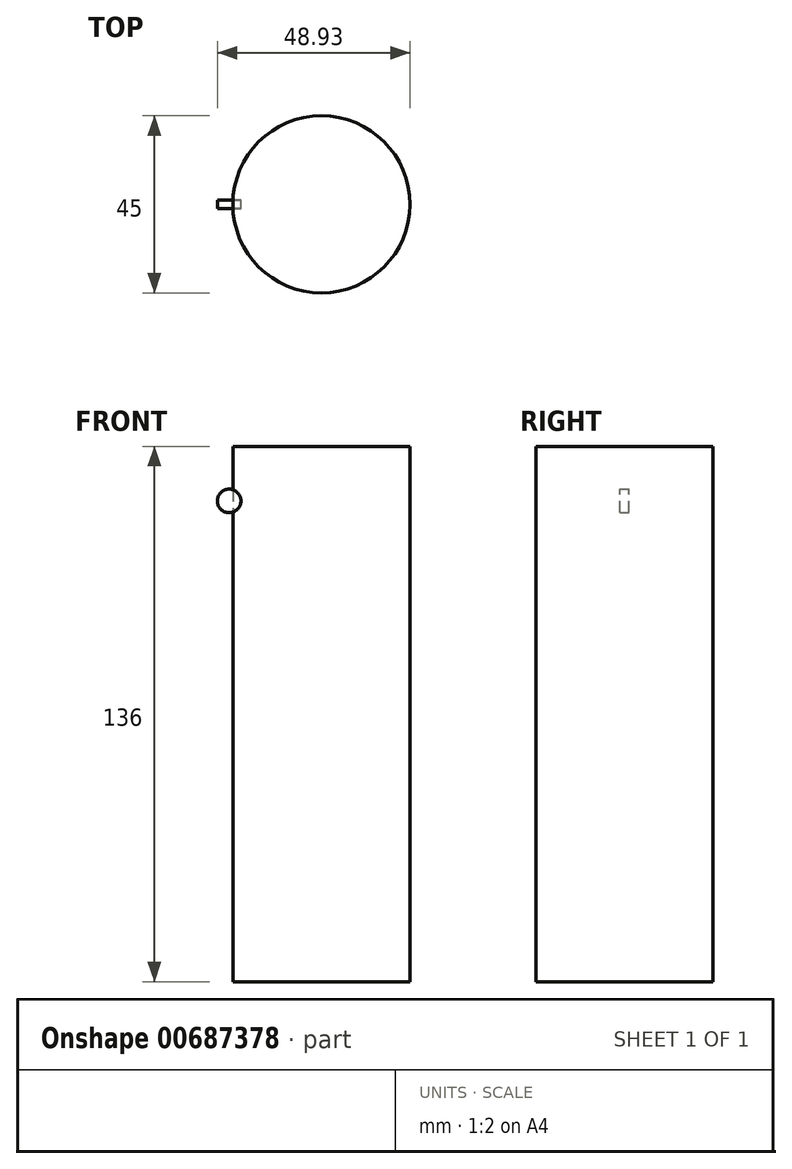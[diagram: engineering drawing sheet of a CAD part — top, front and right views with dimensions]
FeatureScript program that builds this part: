
annotation { "Feature Type Name" : "Feature", "Feature Type Description" : "" }
export const myFeature = defineFeature(function(context is Context, id is Id, definition is map)
    precondition{}
    {
        {
            var Q0;
            Q0=qCreatedBy(makeId("Top.planeOp"),FACE);
            var sketch = newSketch(context, id + "F0", { "sketchPlane" : qUnion([Q0])});
            skCircle(sketch, "E0", {"center": v(0, 0) * mm, "radius": 22.5 * mm});
            skSolve(sketch);
        }
        {
            var Q0;
            Q0 = qSketchRegion(id + "F0", true);
            extrude(context, id + "F1", {"entities" : qUnion([Q0]), "endBound" : BoundingType.SYMMETRIC, "depth" : 136 * mm, "offsetDistance" : 25 * mm});
        }
        {
            var Q0;
            Q0=qCreatedBy(makeId("Front.planeOp"),FACE);
            var sketch = newSketch(context, id + "F2", { "sketchPlane" : qUnion([Q0])});
            skCircle(sketch, "E1", {"center": v(-23.43, 54.15) * mm, "radius": 3 * mm});
            skSolve(sketch);
        }
        {
            var Q0;
            Q0=makeQuery(id+"F2.imprint","IMPRINT",FACE,{"disambiguationData":[TD([[makeQuery(id+"F2.imprint","IMPRINT",EDGE,{"derivedFrom":sQuery(id+"F2.wireOp",EDGE,"E1")}),1.0]])]});
            var Q1;
            Q1=sQuery(id+"F2.wireOp",EDGE,"E1");
            extrude(context, id + "F3", {"entities" : qUnion([Q0]), "surfaceEntities" : qUnion([Q1]), "endBound" : BoundingType.SYMMETRIC, "depth" : 2.2 * mm, "offsetDistance" : 25 * mm});
        }
        {
            var Q0;
            Q0=makeQuery(id+"F3.opExtrude","CAP_EDGE",EDGE,{"disambiguationData":[OSD([sQuery(id+"F2.wireOp",EDGE,"E1")])],"isStart":true});
            var Q1;
            Q1=makeQuery(id+"F1.opExtrude","CAP_EDGE",EDGE,{"disambiguationData":[OSD([sQuery(id+"F0.wireOp",EDGE,"E0")])],"isStart":false});
            revolve(context, id + "F4", {"bodyType" : ToolBodyType.SURFACE, "surfaceEntities" : qUnion([Q0]), "axis" : qUnion([Q1]), "revolveType" : RevolveType.FULL});
        }
    });
